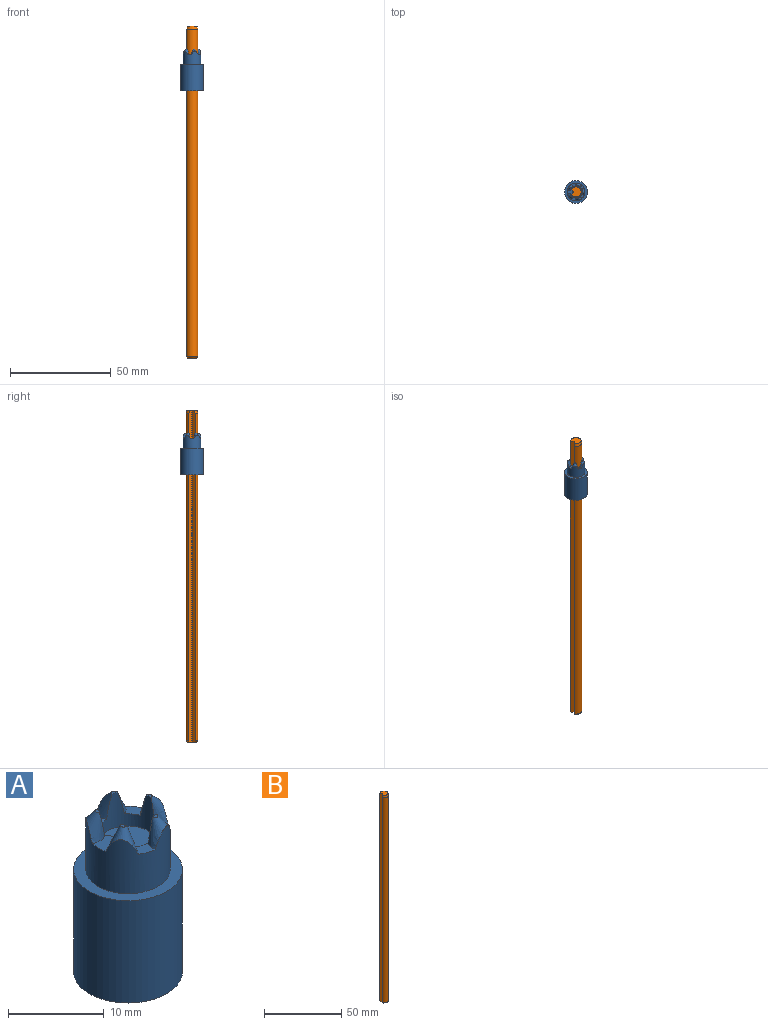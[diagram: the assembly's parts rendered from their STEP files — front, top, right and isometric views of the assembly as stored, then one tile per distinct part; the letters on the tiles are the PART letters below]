
ASSEMBLY  parts=2 mates=1
PART A: 33 faces, bbox 11.7x11.7x21.3 mm
  f0: cylinder r=3.06mm len=6.12mm, axis (0,0,-1), area 44.5mm2, adj f1,f4,f6,f7,f10,f11,f12,f13
  f1: cylinder r=0.15mm len=4.37mm, axis (0,0,-1), area 0.8mm2, adj f0,f2,f17,f32
  f2: plane 3.77x0.68mm, normal (0.71,0.71,0), area 1.9mm2, adj f1,f5,f17,f18,f32
  f3: plane 3.77x0.68mm, normal (0.71,-0.71,0), area 1.9mm2, adj f4,f5,f18,f22,f32
  f4: cylinder r=0.15mm len=4.37mm, axis (0,0,-1), area 0.8mm2, adj f0,f3,f22,f32
  f5: cylinder r=0.9mm len=1.57mm, axis (0,0,-1), area 2.2mm2, adj f2,f3,f18,f32
  f6: cone r=1.8mm half-angle=24.8deg, axis (0.34,0,-0.94), area 9mm2, adj f0,f7,f9,f10,f27
  f7: plane 0.97x0.71mm, normal (0,0,1), area 0.2mm2, adj f0,f6
  f8: cylinder r=3.06mm len=15.9mm, axis (0,0,-1), area 255.9mm2, adj f15,f21,f29,f31
  f9: cylinder r=4.4mm len=8.8mm, axis (0,0,-1), area 159.2mm2, adj f6,f10,f12,f13,f17,f18,f22,f23
  f10: plane 2.32x2.22mm, normal (0,0,1), area 2.2mm2, adj f0,f6,f9,f12
  f11: plane 0.97x0.81mm, normal (0,0,1), area 0.2mm2, adj f0,f12
  f12: cone r=1.8mm half-angle=24.8deg, axis (0.11,0.33,-0.94), area 9mm2, adj f0,f9,f10,f11,f13
  f13: plane 2.2x1.91mm, normal (0,0,1), area 2.2mm2, adj f0,f9,f12,f17
  f14: plane 0.63x0.58mm, normal (0,0,1), area 0.2mm2, adj f0,f17
  f15: cylinder r=0.15mm len=15.9mm, axis (0,0,-1), area 3.1mm2, adj f8,f16,f29,f31
  f16: plane 15.9x0.68mm, normal (0.71,0.71,0), area 15.3mm2, adj f15,f26,f29,f31
  f17: cone r=1.8mm half-angle=24.8deg, axis (-0.28,0.2,-0.94), area 9.8mm2, adj f0,f1,f2,f9,f13,f14,f18
  f18: plane 2.7x2.17mm, normal (0,0,1), area 4.4mm2, adj f2,f3,f5,f9,f17,f22
  f19: plane 0.63x0.58mm, normal (0,0,1), area 0.2mm2, adj f0,f22
  f20: plane 15.9x0.68mm, normal (0.71,-0.71,0), area 15.3mm2, adj f21,f26,f29,f31
  f21: cylinder r=0.15mm len=15.9mm, axis (0,0,-1), area 3.1mm2, adj f8,f20,f29,f31
  f22: cone r=1.8mm half-angle=24.8deg, axis (-0.28,-0.2,-0.94), area 9.8mm2, adj f0,f3,f4,f9,f18,f19,f23
  f23: plane 2.2x1.91mm, normal (0,0,1), area 2.2mm2, adj f0,f9,f22,f24
  f24: cone r=1.8mm half-angle=24.8deg, axis (0.11,-0.33,-0.94), area 9mm2, adj f0,f9,f23,f25,f27
  f25: plane 0.97x0.81mm, normal (0,0,1), area 0.2mm2, adj f0,f24
  f26: cylinder r=0.9mm len=15.9mm, axis (0,0,-1), area 22.5mm2, adj f16,f20,f29,f31
  f27: plane 2.32x2.22mm, normal (0,0,1), area 2.2mm2, adj f0,f6,f9,f24
  f28: cylinder r=5.68mm len=13.05mm, axis (0,0,1), area 465.3mm2, adj f29,f30
  f29: plane 11.35x11.35mm, normal (0,0,-1), area 74.2mm2, adj f8,f15,f16,f20,f21,f26,f28
  f30: plane 11.35x11.35mm, normal (0,0,1), area 40.4mm2, adj f9,f28
  f31: plane 6.12x5.75mm, normal (0,0,-1), area 27mm2, adj f8,f15,f16,f20,f21,f26
  f32: plane 6.12x5.75mm, normal (0,0,1), area 27mm2, adj f0,f1,f2,f3,f4,f5
PART B: 8 faces, bbox 5.6x5.9x165 mm
  f0: plane 165.02x1.36mm, normal (-0.71,0.71,0), area 311.6mm2, adj f1,f3,f4,f5,f6,f7
  f1: cylinder r=2.95mm len=162.9mm, axis (0,0,-1), area 2482.7mm2, adj f0,f2,f6,f7
  f2: plane 165.02x1.36mm, normal (-0.71,-0.71,0), area 311.6mm2, adj f1,f3,f4,f5,f6,f7
  f3: cylinder r=0.3mm len=165mm, axis (0,0,-1), area 77.8mm2, adj f0,f2,f4,f5
  f4: plane 5.09x4.75mm, normal (0,0,1), area 18.2mm2, adj f0,f2,f3,f7
  f5: plane 4.69x4.41mm, normal (0,0,-1), area 15.6mm2, adj f0,f2,f3,f6
  f6: cone r=2.95mm half-angle=45deg, axis (0,0,1), area 11.7mm2, adj f0,f1,f2,f5
  f7: cone r=2.54mm half-angle=15deg, axis (0,0,-1), area 22.2mm2, adj f0,f1,f2,f4
PLACE A at identity fixed
PLACE B t=(0,0,-145.75)mm
MATE fastened B.f1 <-> A.f0  axis (0,0,1) through (0,0,19.25)mm
